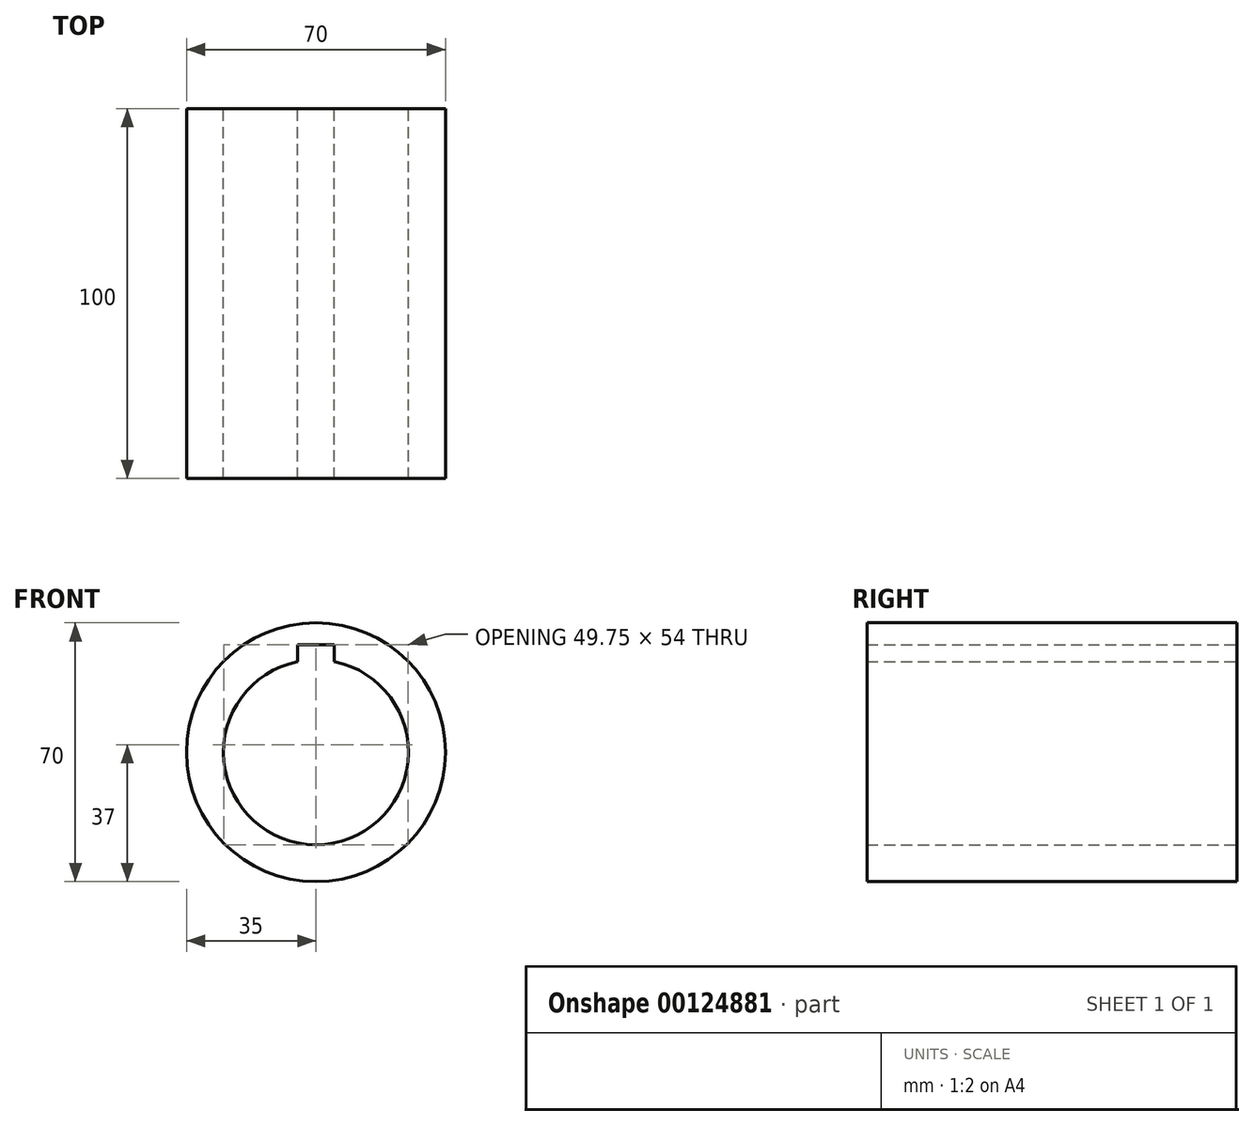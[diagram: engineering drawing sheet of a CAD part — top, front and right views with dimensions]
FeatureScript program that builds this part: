
annotation { "Feature Type Name" : "Feature", "Feature Type Description" : "" }
export const myFeature = defineFeature(function(context is Context, id is Id, definition is map)
    precondition{}
    {
        {
            var Q0;
            Q0=qCreatedBy(makeId("Front.planeOp"),FACE);
            var sketch = newSketch(context, id + "F0", { "sketchPlane" : qUnion([Q0])});
            skCircle(sketch, "E0", {"center": v(0, 0) * mm, "radius": 25 * mm});
            skCircle(sketch, "E1", {"center": v(0, 0) * mm, "radius": 35 * mm});
            skSolve(sketch);
        }
        {
            var Q0;
            Q0=makeQuery(id+"F0.imprint","IMPRINT",FACE,{"disambiguationData":[TD([[makeQuery(id+"F0.imprint","IMPRINT",EDGE,{"derivedFrom":sQuery(id+"F0.wireOp",EDGE,"E0")}),-1.0]])]});
            extrude(context, id + "F1", {"entities" : qUnion([Q0]), "depth" : 100 * mm});
        }
        {
            var Q0;
            Q0=qCreatedBy(makeId("Front.planeOp"),FACE);
            var sketch = newSketch(context, id + "F2", { "sketchPlane" : qUnion([Q0])});
            skCircle(sketch, "E2.0", {"center": v(0, 0) * mm, "radius": 25 * mm, "construction": true});
            skLineSegment(sketch, "E3.bottom", {"start": v(5, 29) * mm, "end": v(-5, 29) * mm});
            skLineSegment(sketch, "E3.top", {"start": v(5, 21) * mm, "end": v(-5, 21) * mm});
            skLineSegment(sketch, "E3.left", {"start": v(5, 29) * mm, "end": v(5, 21) * mm});
            skLineSegment(sketch, "E3.right", {"start": v(-5, 29) * mm, "end": v(-5, 21) * mm});
            skPoint(sketch, "E3.middle", {"position": v(0, 25) * mm});
            skSolve(sketch);
        }
        {
            var Q0;
            Q0=makeQuery(id+"F2.imprint","IMPRINT",FACE,{"disambiguationData":[TD([[makeQuery(id+"F2.imprint","IMPRINT",EDGE,{"derivedFrom":sQuery(id+"F2.wireOp",EDGE,"E3.bottom")}),1.0]])]});
            extrude(context, id + "F3", {"entities" : qUnion([Q0]), "operationType" : NewBodyOperationType.REMOVE, "endBound" : BoundingType.THROUGH_ALL, "depth" : 25 * mm});
        }
    });
